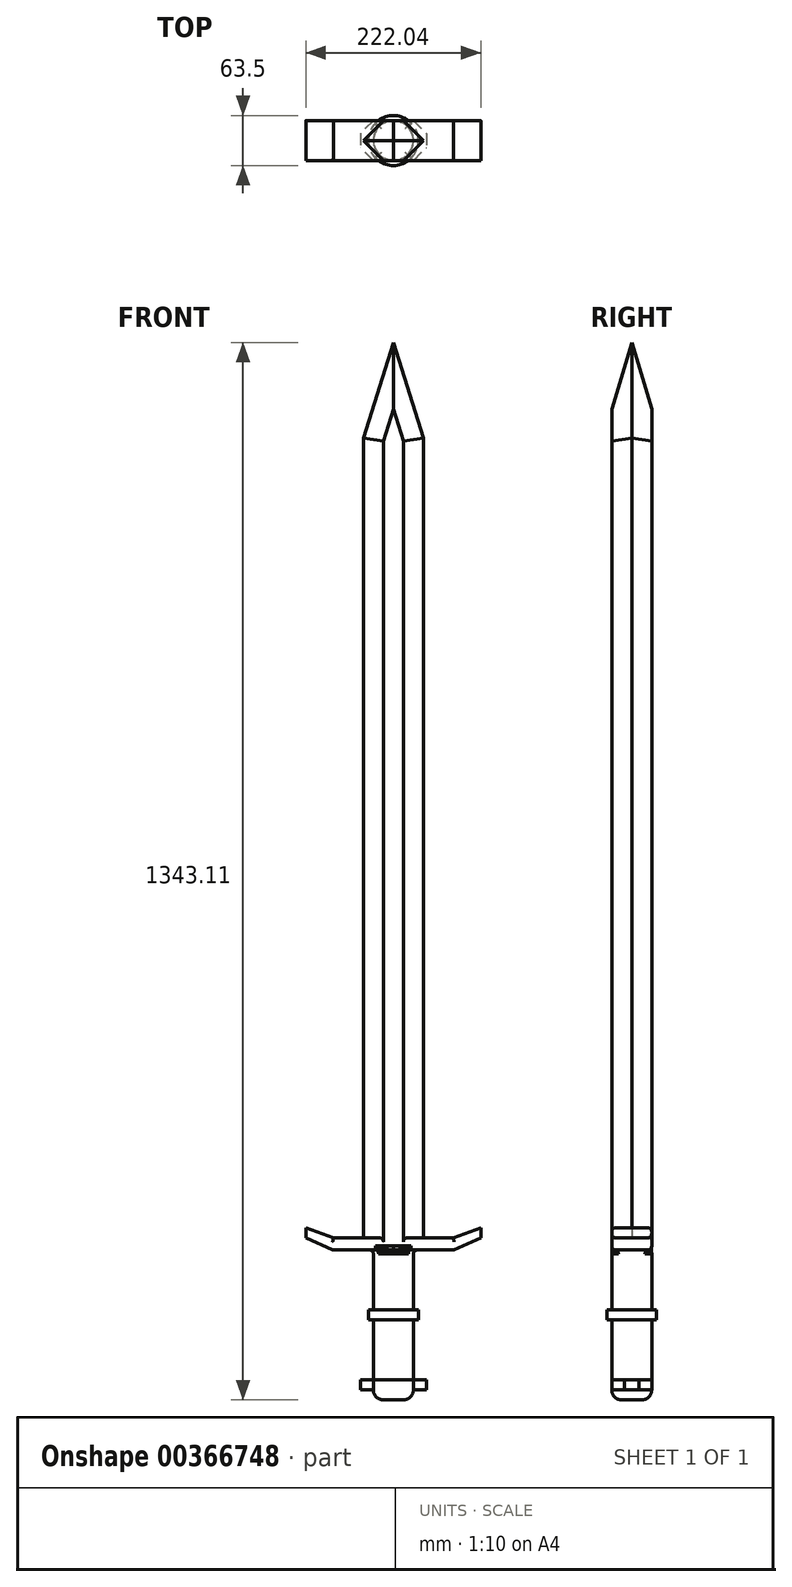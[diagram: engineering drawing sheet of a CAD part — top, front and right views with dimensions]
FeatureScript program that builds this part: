
annotation { "Feature Type Name" : "Feature", "Feature Type Description" : "" }
export const myFeature = defineFeature(function(context is Context, id is Id, definition is map)
    precondition{}
    {
        {
            var Q0;
            Q0=qCreatedBy(makeId("Front.planeOp"),FACE);
            var sketch = newSketch(context, id + "F0", { "sketchPlane" : qUnion([Q0])});
            skLineSegment(sketch, "E0.bottom", {"start": v(25.4, -38.1) * mm, "end": v(-25.4, -38.1) * mm});
            skLineSegment(sketch, "E0.top", {"start": v(25.4, 38.1) * mm, "end": v(-25.4, 38.1) * mm});
            skLineSegment(sketch, "E0.left", {"start": v(25.4, -38.1) * mm, "end": v(25.4, 38.1) * mm});
            skLineSegment(sketch, "E0.right", {"start": v(-25.4, -38.1) * mm, "end": v(-25.4, 38.1) * mm});
            skPoint(sketch, "E0.middle", {"position": v(0, 0) * mm});
            skSolve(sketch);
        }
        {
            var Q0;
            Q0 = qSketchRegion(id + "F0", true);
            extrude(context, id + "F1", {"entities" : qUnion([Q0]), "depth" : 50.8 * mm});
        }
        {
            var Q0;
            Q0=makeQuery(id+"F1.opExtrude","SWEPT_FACE",FACE,{"disambiguationData":[OSD([sQuery(id+"F0.wireOp",EDGE,"E0.top")])]});
            var sketch = newSketch(context, id + "F2", { "sketchPlane" : qUnion([Q0])});
            skLineSegment(sketch, "E1", {"start": v(0, 0) * mm, "end": v(0, -50.8) * mm});
            skLineSegment(sketch, "E2", {"start": v(0, -50.8) * mm, "end": v(0, -25.4) * mm});
            skCircle(sketch, "E3", {"center": v(0, -25.4) * mm, "radius": 31.75 * mm});
            skSolve(sketch);
        }
        {
            var Q0;
            Q0 = qSketchRegion(id + "F2", true);
            extrude(context, id + "F3", {"entities" : qUnion([Q0]), "operationType" : NewBodyOperationType.ADD, "depth" : 12.7 * mm});
        }
        {
            var Q0;
            Q0=makeQuery(id+"F1.opExtrude","CAP_FACE",FACE,{"disambiguationData":[OSD([sQuery(id+"F0.wireOp",EDGE,"E0.bottom"),sQuery(id+"F0.wireOp",EDGE,"E0.top"),sQuery(id+"F0.wireOp",EDGE,"E0.left"),sQuery(id+"F0.wireOp",EDGE,"E0.right")])],"isStart":false});
            var sketch = newSketch(context, id + "F4", { "sketchPlane" : qUnion([Q0])});
            skLineSegment(sketch, "E4", {"start": v(-25.4, 38.1) * mm, "end": v(-25.4, 50.8) * mm});
            skLineSegment(sketch, "E5", {"start": v(-25.4, 50.8) * mm, "end": v(25.4, 50.8) * mm});
            skLineSegment(sketch, "E6", {"start": v(25.4, 50.8) * mm, "end": v(25.4, 127) * mm});
            skLineSegment(sketch, "E7", {"start": v(-25.4, 50.8) * mm, "end": v(-25.4, 127) * mm});
            skLineSegment(sketch, "E8", {"start": v(-25.4, 127) * mm, "end": v(25.4, 127) * mm});
            skSolve(sketch);
        }
        {
            var Q0;
            Q0 = qSketchRegion(id + "F4", true);
            extrude(context, id + "F5", {"entities" : qUnion([Q0]), "operationType" : NewBodyOperationType.ADD, "depth" : -50.8 * mm});
        }
        {
            var Q0;
            Q0=makeQuery(id+"F1.opExtrude","CAP_FACE",FACE,{"disambiguationData":[OSD([sQuery(id+"F0.wireOp",EDGE,"E0.bottom"),sQuery(id+"F0.wireOp",EDGE,"E0.top"),sQuery(id+"F0.wireOp",EDGE,"E0.left"),sQuery(id+"F0.wireOp",EDGE,"E0.right")])],"isStart":false});
            var sketch = newSketch(context, id + "F6", { "sketchPlane" : qUnion([Q0])});
            skLineSegment(sketch, "E9", {"start": v(25.4, -38.1) * mm, "end": v(50.8, -38.1) * mm});
            skLineSegment(sketch, "E10", {"start": v(-25.4, -38.1) * mm, "end": v(-50.8, -38.1) * mm});
            skLineSegment(sketch, "E11", {"start": v(-50.8, -38.1) * mm, "end": v(-50.8, -50.8) * mm});
            skLineSegment(sketch, "E12", {"start": v(-50.8, -50.8) * mm, "end": v(0, -50.8) * mm});
            skLineSegment(sketch, "E13", {"start": v(0, -50.8) * mm, "end": v(50.8, -50.8) * mm});
            skLineSegment(sketch, "E14", {"start": v(50.8, -50.8) * mm, "end": v(50.8, -38.1) * mm});
            skLineSegment(sketch, "E15", {"start": v(-25.4, -50.8) * mm, "end": v(-25.4, -63.5) * mm});
            skLineSegment(sketch, "E16", {"start": v(-25.4, -63.5) * mm, "end": v(0, -63.5) * mm});
            skLineSegment(sketch, "E17.MirrorCS", {"start": v(25.4, -63.5) * mm, "end": v(0, -63.5) * mm});
            skLineSegment(sketch, "E18.MirrorCS", {"start": v(25.4, -50.8) * mm, "end": v(25.4, -63.5) * mm});
            skSolve(sketch);
        }
        {
            var Q0;
            Q0 = qSketchRegion(id + "F6", true);
            var Q1;
            Q1=makeQuery(id+"F6.imprint","IMPRINT",FACE,{"disambiguationData":[TD([[makeQuery(id+"F6.imprint","IMPRINT",EDGE,{"derivedFrom":sQuery(id+"F6.wireOp",EDGE,"E9")}),-1.0]])]});
            extrude(context, id + "F7", {"entities" : qUnion([Q0, Q1]), "operationType" : NewBodyOperationType.ADD, "depth" : -50.8 * mm});
        }
        {
            var Q0;
            Q0=makeQuery(id+"F5.opExtrude","CAP_FACE",FACE,{"disambiguationData":[OSD([sQuery(id+"F4.wireOp",EDGE,"E5"),sQuery(id+"F4.wireOp",EDGE,"E6"),sQuery(id+"F4.wireOp",EDGE,"E7"),sQuery(id+"F4.wireOp",EDGE,"E8")])],"isStart":true});
            var sketch = newSketch(context, id + "F8", { "sketchPlane" : qUnion([Q0])});
            skLineSegment(sketch, "E19", {"start": v(-25.4, 127) * mm, "end": v(-76.2, 127) * mm});
            skLineSegment(sketch, "E20", {"start": v(-76.2, 127) * mm, "end": v(-111.02, 142.46) * mm});
            skLineSegment(sketch, "E21.MirrorCS", {"start": v(25.4, 127) * mm, "end": v(76.2, 127) * mm});
            skLineSegment(sketch, "E22.MirrorCS", {"start": v(76.2, 127) * mm, "end": v(111.02, 142.46) * mm});
            skLineSegment(sketch, "E23", {"start": v(-76.2, 127) * mm, "end": v(-76.2, 142.46) * mm});
            skLineSegment(sketch, "E24", {"start": v(76.2, 127) * mm, "end": v(76.2, 142.46) * mm});
            skLineSegment(sketch, "E25", {"start": v(-25.4, 127) * mm, "end": v(-25.4, 142.46) * mm});
            skLineSegment(sketch, "E26", {"start": v(25.4, 127) * mm, "end": v(25.4, 142.46) * mm});
            skLineSegment(sketch, "E27", {"start": v(-111.02, 142.46) * mm, "end": v(-111.02, 155.16) * mm});
            skLineSegment(sketch, "E28", {"start": v(-111.02, 155.16) * mm, "end": v(-76.2, 142.46) * mm});
            skLineSegment(sketch, "E29", {"start": v(-25.4, 142.46) * mm, "end": v(-76.2, 142.46) * mm});
            skLineSegment(sketch, "E30", {"start": v(25.4, 142.46) * mm, "end": v(-25.4, 142.46) * mm});
            skLineSegment(sketch, "E31", {"start": v(25.4, 142.46) * mm, "end": v(76.2, 142.46) * mm});
            skLineSegment(sketch, "E32.MirrorCS", {"start": v(111.02, 142.46) * mm, "end": v(111.02, 155.16) * mm});
            skLineSegment(sketch, "E33.MirrorCS", {"start": v(111.02, 155.16) * mm, "end": v(76.2, 142.46) * mm});
            skSolve(sketch);
        }
        {
            var Q0;
            Q0 = qSketchRegion(id + "F8", true);
            var Q1;
            Q1=makeQuery(id+"F8.imprint","IMPRINT",FACE,{"disambiguationData":[TD([[makeQuery(id+"F8.imprint","IMPRINT",EDGE,{"derivedFrom":sQuery(id+"F8.wireOp",EDGE,"E25")}),-1.0]])]});
            extrude(context, id + "F9", {"entities" : qUnion([Q0, Q1]), "operationType" : NewBodyOperationType.ADD, "depth" : -50.8 * mm});
        }
        {
            var Q0;
            {var subQ0=sQuery(id+"F4.wireOp",EDGE,"E8");Q0=makeQuery(id+"F9.boolean.opBoolean","MERGE",FACE,{"derivedFrom":[makeQuery(id+"F5.opExtrude","CAP_FACE",FACE,{"disambiguationData":[OSD([sQuery(id+"F4.wireOp",EDGE,"E5"),sQuery(id+"F4.wireOp",EDGE,"E6"),sQuery(id+"F4.wireOp",EDGE,"E7"),subQ0])],"isStart":true}),makeQuery(id+"F9.opExtrude","CAP_FACE",FACE,{"disambiguationData":[OSD([subQ0,sQuery(id+"F8.wireOp",EDGE,"E19"),sQuery(id+"F8.wireOp",EDGE,"E20"),sQuery(id+"F8.wireOp",EDGE,"E21.MirrorCS"),sQuery(id+"F8.wireOp",EDGE,"E22.MirrorCS"),sQuery(id+"F8.wireOp",EDGE,"E27"),sQuery(id+"F8.wireOp",EDGE,"E28"),sQuery(id+"F8.wireOp",EDGE,"E29"),sQuery(id+"F8.wireOp",EDGE,"E30"),sQuery(id+"F8.wireOp",EDGE,"E31"),sQuery(id+"F8.wireOp",EDGE,"E32.MirrorCS"),sQuery(id+"F8.wireOp",EDGE,"E33.MirrorCS")])],"isStart":true})]});}
            var sketch = newSketch(context, id + "F10", { "sketchPlane" : qUnion([Q0])});
            skLineSegment(sketch, "E34", {"start": v(-76.2, 142.46) * mm, "end": v(0, 142.46) * mm});
            skLineSegment(sketch, "E35", {"start": v(0, 142.46) * mm, "end": v(76.2, 142.46) * mm});
            skLineSegment(sketch, "E36", {"start": v(76.2, 142.46) * mm, "end": v(38.1, 142.46) * mm});
            skLineSegment(sketch, "E37", {"start": v(38.1, 142.46) * mm, "end": v(-38.1, 142.46) * mm});
            skLineSegment(sketch, "E38", {"start": v(-38.1, 142.46) * mm, "end": v(0, 142.46) * mm});
            skLineSegment(sketch, "E39", {"start": v(0, 142.46) * mm, "end": v(-19.05, 142.46) * mm});
            skLineSegment(sketch, "E40", {"start": v(-19.05, 142.46) * mm, "end": v(38.1, 142.46) * mm});
            skLineSegment(sketch, "E41", {"start": v(38.1, 142.46) * mm, "end": v(0, 142.46) * mm});
            skLineSegment(sketch, "E42", {"start": v(0, 142.46) * mm, "end": v(19.05, 142.46) * mm});
            skLineSegment(sketch, "E43", {"start": v(-38.1, 142.46) * mm, "end": v(-38.1, 1158.46) * mm});
            skLineSegment(sketch, "E44.MirrorCS", {"start": v(38.1, 142.46) * mm, "end": v(38.1, 1158.46) * mm});
            skLineSegment(sketch, "E45", {"start": v(-38.1, 1158.46) * mm, "end": v(0, 1279.61) * mm});
            skLineSegment(sketch, "E46", {"start": v(0, 1279.61) * mm, "end": v(38.1, 1158.46) * mm});
            skSolve(sketch);
        }
        {
            var Q0;
            Q0 = qSketchRegion(id + "F10", true);
            extrude(context, id + "F11", {"entities" : qUnion([Q0]), "operationType" : NewBodyOperationType.ADD, "depth" : -50.8 * mm});
        }
        {
            var Q0;
            Q0=makeQuery(id+"F5.opExtrude","CAP_EDGE",EDGE,{"disambiguationData":[OSD([sQuery(id+"F4.wireOp",EDGE,"E7")])],"isStart":true});
            var Q1;
            Q1=makeQuery(id+"F5.opExtrude","CAP_EDGE",EDGE,{"disambiguationData":[OSD([sQuery(id+"F4.wireOp",EDGE,"E6")])],"isStart":true});
            var Q2;
            Q2=makeQuery(id+"F5.opExtrude","CAP_EDGE",EDGE,{"disambiguationData":[OSD([sQuery(id+"F4.wireOp",EDGE,"E7")])],"isStart":false});
            var Q3;
            Q3=makeQuery(id+"F1.opExtrude","CAP_EDGE",EDGE,{"disambiguationData":[OSD([sQuery(id+"F0.wireOp",EDGE,"E0.right")])],"isStart":true});
            var Q4;
            Q4=makeQuery(id+"F1.opExtrude","CAP_EDGE",EDGE,{"disambiguationData":[OSD([sQuery(id+"F0.wireOp",EDGE,"E0.right")])],"isStart":false});
            var Q5;
            Q5=makeQuery(id+"F1.opExtrude","CAP_EDGE",EDGE,{"disambiguationData":[OSD([sQuery(id+"F0.wireOp",EDGE,"E0.left")])],"isStart":false});
            var Q6;
            Q6=makeQuery(id+"F5.opExtrude","CAP_EDGE",EDGE,{"disambiguationData":[OSD([sQuery(id+"F4.wireOp",EDGE,"E6")])],"isStart":false});
            var Q7;
            Q7=makeQuery(id+"F1.opExtrude","CAP_EDGE",EDGE,{"disambiguationData":[OSD([sQuery(id+"F0.wireOp",EDGE,"E0.left")])],"isStart":true});
            fillet(context, id + "F12", {"entities" : qUnion([Q0, Q1, Q2, Q3, Q4, Q5, Q6, Q7]), "radius" : 25.4 * mm, "tangentPropagation" : true, "allowEdgeOverflow" : false});
        }
        {
            var Q0;
            Q0=makeQuery(id+"F7.opExtrude","CAP_EDGE",EDGE,{"disambiguationData":[OSD([sQuery(id+"F6.wireOp",EDGE,"E11")])],"isStart":false});
            var Q1;
            Q1=makeQuery(id+"F7.opExtrude","CAP_EDGE",EDGE,{"disambiguationData":[OSD([sQuery(id+"F6.wireOp",EDGE,"E14")])],"isStart":false});
            var Q2;
            Q2=makeQuery(id+"F7.opExtrude","CAP_EDGE",EDGE,{"disambiguationData":[OSD([sQuery(id+"F6.wireOp",EDGE,"E14")])],"isStart":true});
            var Q3;
            Q3=makeQuery(id+"F7.opExtrude","CAP_EDGE",EDGE,{"disambiguationData":[OSD([sQuery(id+"F6.wireOp",EDGE,"E11")])],"isStart":true});
            chamfer(context, id + "F13", {"entities" : qUnion([Q0, Q1, Q2, Q3]), "width" : 25.4 * mm, "tangentPropagation" : true});
        }
        {
            var Q0;
            {var subQ0=sQuery(id+"F6.wireOp",EDGE,"E14");Q0=makeQuery(id+"F13.opChamfer","BLEND_EDGE",EDGE,{"blendedFrom":[makeQuery(id+"F7.opExtrude","CAP_EDGE",EDGE,{"disambiguationData":[OSD([subQ0])],"isStart":true}),makeQuery(id+"F7.opExtrude","CAP_EDGE",EDGE,{"disambiguationData":[OSD([subQ0])],"isStart":false})],"blendedInto":[]});}
            var Q1;
            {var subQ0=sQuery(id+"F6.wireOp",EDGE,"E11");Q1=makeQuery(id+"F13.opChamfer","BLEND_EDGE",EDGE,{"blendedFrom":[makeQuery(id+"F7.opExtrude","CAP_EDGE",EDGE,{"disambiguationData":[OSD([subQ0])],"isStart":true}),makeQuery(id+"F7.opExtrude","CAP_EDGE",EDGE,{"disambiguationData":[OSD([subQ0])],"isStart":false})],"blendedInto":[]});}
            chamfer(context, id + "F14", {"entities" : qUnion([Q0, Q1]), "width" : 12.7 * mm, "tangentPropagation" : true});
        }
        {
            var Q0;
            Q0=makeQuery(id+"F7.opExtrude","SWEPT_EDGE",EDGE,{"disambiguationData":[OSD([sQuery(id+"F6.wireOp",EDGE,"E15"),sQuery(id+"F6.wireOp",EDGE,"E16")])]});
            var Q1;
            Q1=makeQuery(id+"F7.opExtrude","CAP_EDGE",EDGE,{"disambiguationData":[OSD([sQuery(id+"F6.wireOp",EDGE,"E16"),sQuery(id+"F6.wireOp",EDGE,"E17.MirrorCS")])],"isStart":false});
            var Q2;
            Q2=makeQuery(id+"F7.opExtrude","SWEPT_EDGE",EDGE,{"disambiguationData":[OSD([sQuery(id+"F6.wireOp",EDGE,"E17.MirrorCS"),sQuery(id+"F6.wireOp",EDGE,"E18.MirrorCS")])]});
            var Q3;
            Q3=makeQuery(id+"F7.opExtrude","CAP_EDGE",EDGE,{"disambiguationData":[OSD([sQuery(id+"F6.wireOp",EDGE,"E16"),sQuery(id+"F6.wireOp",EDGE,"E17.MirrorCS")])],"isStart":true});
            fillet(context, id + "F15", {"entities" : qUnion([Q0, Q1, Q2, Q3]), "radius" : 12.7 * mm, "tangentPropagation" : true, "allowEdgeOverflow" : false});
        }
        {
            var Q0;
            Q0=makeQuery(id+"F11.opExtrude","CAP_EDGE",EDGE,{"disambiguationData":[OSD([sQuery(id+"F10.wireOp",EDGE,"E43")])],"isStart":true});
            var Q1;
            Q1=makeQuery(id+"F11.opExtrude","CAP_EDGE",EDGE,{"disambiguationData":[OSD([sQuery(id+"F10.wireOp",EDGE,"E44.MirrorCS")])],"isStart":true});
            var Q2;
            Q2=makeQuery(id+"F11.opExtrude","CAP_EDGE",EDGE,{"disambiguationData":[OSD([sQuery(id+"F10.wireOp",EDGE,"E43")])],"isStart":false});
            var Q3;
            Q3=makeQuery(id+"F11.opExtrude","CAP_EDGE",EDGE,{"disambiguationData":[OSD([sQuery(id+"F10.wireOp",EDGE,"E46")])],"isStart":true});
            var Q4;
            Q4=makeQuery(id+"F11.opExtrude","CAP_EDGE",EDGE,{"disambiguationData":[OSD([sQuery(id+"F10.wireOp",EDGE,"E45")])],"isStart":true});
            var Q5;
            Q5=makeQuery(id+"F11.opExtrude","CAP_EDGE",EDGE,{"disambiguationData":[OSD([sQuery(id+"F10.wireOp",EDGE,"E45")])],"isStart":false});
            var Q6;
            Q6=makeQuery(id+"F11.opExtrude","CAP_EDGE",EDGE,{"disambiguationData":[OSD([sQuery(id+"F10.wireOp",EDGE,"E46")])],"isStart":false});
            var Q7;
            Q7=makeQuery(id+"F11.opExtrude","CAP_EDGE",EDGE,{"disambiguationData":[OSD([sQuery(id+"F10.wireOp",EDGE,"E44.MirrorCS")])],"isStart":false});
            chamfer(context, id + "F16", {"entities" : qUnion([Q0, Q1, Q2, Q3, Q4, Q5, Q6, Q7]), "chamferType" : ChamferType.OFFSET_ANGLE, "width" : 25.4 * mm, "oppositeDirection" : false, "angle" : 45 * degree, "tangentPropagation" : true});
        }
        {
            var Q0;
            {var subQ0=sQuery(id+"F8.wireOp",EDGE,"E31");var subQ1=sQuery(id+"F8.wireOp",EDGE,"E30");var subQ2=sQuery(id+"F8.wireOp",EDGE,"E29");var subQ4=sQuery(id+"F8.wireOp",EDGE,"E33.MirrorCS");Q0=makeQuery(id+"F11.boolean.opBoolean","SPLIT",EDGE,{"disambiguationData":[TD([makeQuery(id+"F9.opExtrude","SWEPT_FACE",FACE,{"disambiguationData":[OSD([subQ4])]})])],"derivedFrom":makeQuery(id+"F9.opExtrude","CAP_EDGE",EDGE,{"disambiguationData":[OSD([subQ2,subQ1,subQ0])],"isStart":false})});}
            var Q1;
            {var subQ0=sQuery(id+"F8.wireOp",EDGE,"E31");var subQ1=sQuery(id+"F8.wireOp",EDGE,"E30");var subQ2=sQuery(id+"F8.wireOp",EDGE,"E29");var subQ4=sQuery(id+"F8.wireOp",EDGE,"E28");Q1=makeQuery(id+"F11.boolean.opBoolean","SPLIT",EDGE,{"disambiguationData":[TD([makeQuery(id+"F9.opExtrude","SWEPT_FACE",FACE,{"disambiguationData":[OSD([subQ4])]})])],"derivedFrom":makeQuery(id+"F9.opExtrude","CAP_EDGE",EDGE,{"disambiguationData":[OSD([subQ2,subQ1,subQ0])],"isStart":false})});}
            var Q2;
            Q2=makeQuery(id+"F9.opExtrude","CAP_EDGE",EDGE,{"disambiguationData":[OSD([sQuery(id+"F8.wireOp",EDGE,"E20")])],"isStart":false});
            var Q3;
            Q3=makeQuery(id+"F9.opExtrude","CAP_EDGE",EDGE,{"disambiguationData":[OSD([sQuery(id+"F8.wireOp",EDGE,"E28")])],"isStart":false});
            var Q4;
            {var subQ0=sQuery(id+"F8.wireOp",EDGE,"E21.MirrorCS");var subQ1=sQuery(id+"F8.wireOp",EDGE,"E19");var subQ2=sQuery(id+"F4.wireOp",EDGE,"E8");var subQ4=sQuery(id+"F4.wireOp",EDGE,"E6");Q4=makeQuery(id+"F9.boolean.opBoolean","SPLIT",EDGE,{"disambiguationData":[TD([makeQuery(id+"F5.opExtrude","SWEPT_FACE",FACE,{"disambiguationData":[OSD([subQ4])]})])],"derivedFrom":makeQuery(id+"F9.opExtrude","CAP_EDGE",EDGE,{"disambiguationData":[OSD([subQ2,subQ1,subQ0])],"isStart":false})});}
            var Q5;
            {var subQ0=sQuery(id+"F8.wireOp",EDGE,"E21.MirrorCS");var subQ1=sQuery(id+"F8.wireOp",EDGE,"E19");var subQ2=sQuery(id+"F4.wireOp",EDGE,"E8");var subQ4=sQuery(id+"F4.wireOp",EDGE,"E7");Q5=makeQuery(id+"F9.boolean.opBoolean","SPLIT",EDGE,{"disambiguationData":[TD([makeQuery(id+"F5.opExtrude","SWEPT_FACE",FACE,{"disambiguationData":[OSD([subQ4])]})])],"derivedFrom":makeQuery(id+"F9.opExtrude","CAP_EDGE",EDGE,{"disambiguationData":[OSD([subQ2,subQ1,subQ0])],"isStart":false})});}
            var Q6;
            Q6=makeQuery(id+"F9.opExtrude","CAP_EDGE",EDGE,{"disambiguationData":[OSD([sQuery(id+"F8.wireOp",EDGE,"E22.MirrorCS")])],"isStart":false});
            var Q7;
            Q7=makeQuery(id+"F9.opExtrude","CAP_EDGE",EDGE,{"disambiguationData":[OSD([sQuery(id+"F8.wireOp",EDGE,"E33.MirrorCS")])],"isStart":false});
            var Q8;
            {var subQ0=sQuery(id+"F8.wireOp",EDGE,"E33.MirrorCS");var subQ2=sQuery(id+"F8.wireOp",EDGE,"E31");var subQ3=sQuery(id+"F8.wireOp",EDGE,"E30");var subQ4=sQuery(id+"F8.wireOp",EDGE,"E29");Q8=makeQuery(id+"F11.boolean.opBoolean","SPLIT",EDGE,{"disambiguationData":[TD([makeQuery(id+"F9.opExtrude","SWEPT_FACE",FACE,{"disambiguationData":[OSD([subQ0])]})])],"derivedFrom":makeQuery(id+"F9.opExtrude","CAP_EDGE",EDGE,{"disambiguationData":[OSD([subQ4,subQ3,subQ2])],"isStart":true})});}
            var Q9;
            {var subQ0=sQuery(id+"F8.wireOp",EDGE,"E31");var subQ1=sQuery(id+"F8.wireOp",EDGE,"E30");var subQ2=sQuery(id+"F8.wireOp",EDGE,"E29");var subQ3=sQuery(id+"F8.wireOp",EDGE,"E28");Q9=makeQuery(id+"F11.boolean.opBoolean","SPLIT",EDGE,{"disambiguationData":[TD([makeQuery(id+"F9.opExtrude","SWEPT_FACE",FACE,{"disambiguationData":[OSD([subQ3])]})])],"derivedFrom":makeQuery(id+"F9.opExtrude","CAP_EDGE",EDGE,{"disambiguationData":[OSD([subQ2,subQ1,subQ0])],"isStart":true})});}
            var Q10;
            Q10=makeQuery(id+"F9.opExtrude","CAP_EDGE",EDGE,{"disambiguationData":[OSD([sQuery(id+"F8.wireOp",EDGE,"E28")])],"isStart":true});
            var Q11;
            Q11=makeQuery(id+"F9.opExtrude","CAP_EDGE",EDGE,{"disambiguationData":[OSD([sQuery(id+"F8.wireOp",EDGE,"E33.MirrorCS")])],"isStart":true});
            var Q12;
            Q12=makeQuery(id+"F9.opExtrude","CAP_EDGE",EDGE,{"disambiguationData":[OSD([sQuery(id+"F8.wireOp",EDGE,"E20")])],"isStart":true});
            var Q13;
            {var subQ8=sQuery(id+"F8.wireOp",EDGE,"E21.MirrorCS");var subQ10=sQuery(id+"F8.wireOp",EDGE,"E19");var subQ11=sQuery(id+"F4.wireOp",EDGE,"E8");var subQ12=sQuery(id+"F4.wireOp",EDGE,"E7");Q13=makeQuery(id+"F9.boolean.opBoolean","SPLIT",FACE,{"disambiguationData":[TD([makeQuery(id+"F5.opExtrude","SWEPT_FACE",FACE,{"disambiguationData":[OSD([subQ12])]})])],"derivedFrom":makeQuery(id+"F9.opExtrude","SWEPT_FACE",FACE,{"disambiguationData":[OSD([subQ11,subQ10,subQ8])]})});}
            var Q14;
            {var subQ8=sQuery(id+"F8.wireOp",EDGE,"E21.MirrorCS");var subQ10=sQuery(id+"F8.wireOp",EDGE,"E19");var subQ11=sQuery(id+"F4.wireOp",EDGE,"E8");var subQ12=sQuery(id+"F4.wireOp",EDGE,"E6");Q14=makeQuery(id+"F9.boolean.opBoolean","SPLIT",FACE,{"disambiguationData":[TD([makeQuery(id+"F5.opExtrude","SWEPT_FACE",FACE,{"disambiguationData":[OSD([subQ12])]})])],"derivedFrom":makeQuery(id+"F9.opExtrude","SWEPT_FACE",FACE,{"disambiguationData":[OSD([subQ11,subQ10,subQ8])]})});}
            var Q15;
            Q15=makeQuery(id+"F9.opExtrude","CAP_EDGE",EDGE,{"disambiguationData":[OSD([sQuery(id+"F8.wireOp",EDGE,"E22.MirrorCS")])],"isStart":true});
            fillet(context, id + "F17", {"entities" : qUnion([Q0, Q1, Q2, Q3, Q4, Q5, Q6, Q7, Q8, Q9, Q10, Q11, Q12, Q13, Q14, Q15]), "radius" : 5.08 * mm, "tangentPropagation" : true, "allowEdgeOverflow" : false});
        }
    });
